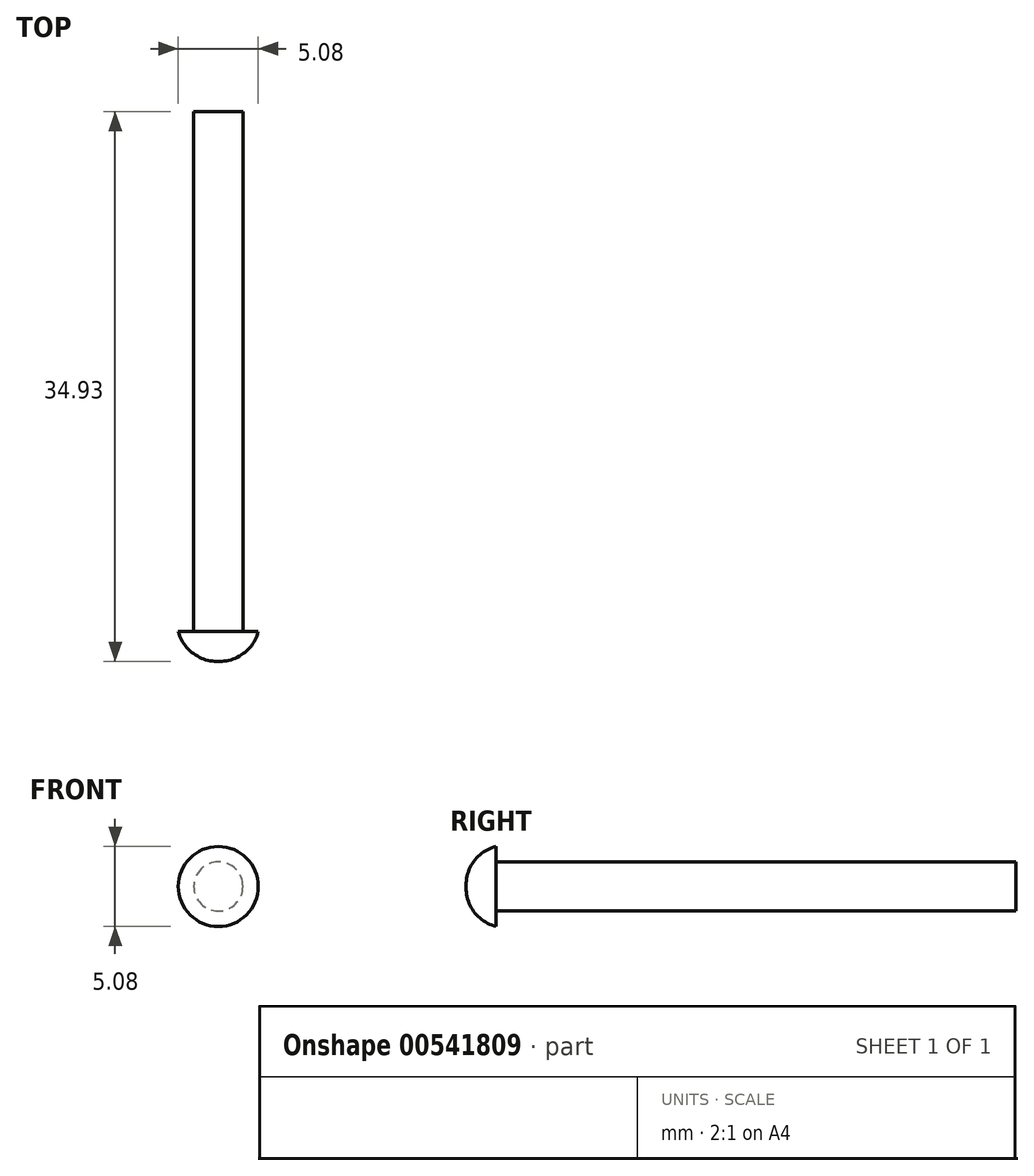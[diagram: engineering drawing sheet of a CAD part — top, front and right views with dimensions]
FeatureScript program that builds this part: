
annotation { "Feature Type Name" : "Feature", "Feature Type Description" : "" }
export const myFeature = defineFeature(function(context is Context, id is Id, definition is map)
    precondition{}
    {
        {
            var Q0;
            Q0=qCreatedBy(makeId("Front.planeOp"),FACE);
            var sketch = newSketch(context, id + "F0", { "sketchPlane" : qUnion([Q0])});
            skCircle(sketch, "E0", {"center": v(10.2, 6.34) * mm, "radius": 1.56 * mm});
            skSolve(sketch);
        }
        {
            var Q0;
            Q0 = qSketchRegion(id + "F0", true);
            extrude(context, id + "F1", {"entities" : qUnion([Q0]), "depth" : 33.02 * mm, "offsetDistance" : 25.4 * mm});
        }
        {
            var Q0;
            Q0=makeQuery(id+"F1.opExtrude","CAP_FACE",FACE,{"disambiguationData":[OSD([sQuery(id+"F0.wireOp",EDGE,"E0")])],"isStart":false});
            var sketch = newSketch(context, id + "F2", { "sketchPlane" : qUnion([Q0])});
            skCircle(sketch, "E1", {"center": v(10.2, 6.34) * mm, "radius": 2.54 * mm});
            skSolve(sketch);
        }
        {
            var Q0;
            Q0 = qSketchRegion(id + "F2", true);
            extrude(context, id + "F3", {"entities" : qUnion([Q0]), "operationType" : NewBodyOperationType.ADD, "depth" : 1.9 * mm, "offsetDistance" : 25.4 * mm});
        }
        {
            var Q0;
            Q0=makeQuery(id+"F3.opExtrude","CAP_EDGE",EDGE,{"disambiguationData":[OSD([sQuery(id+"F2.wireOp",EDGE,"E1")])],"isStart":false});
            fillet(context, id + "F4", {"entities" : qUnion([Q0]), "radius" : 2.54 * mm, "tangentPropagation" : true, "allowEdgeOverflow" : false});
        }
    });
